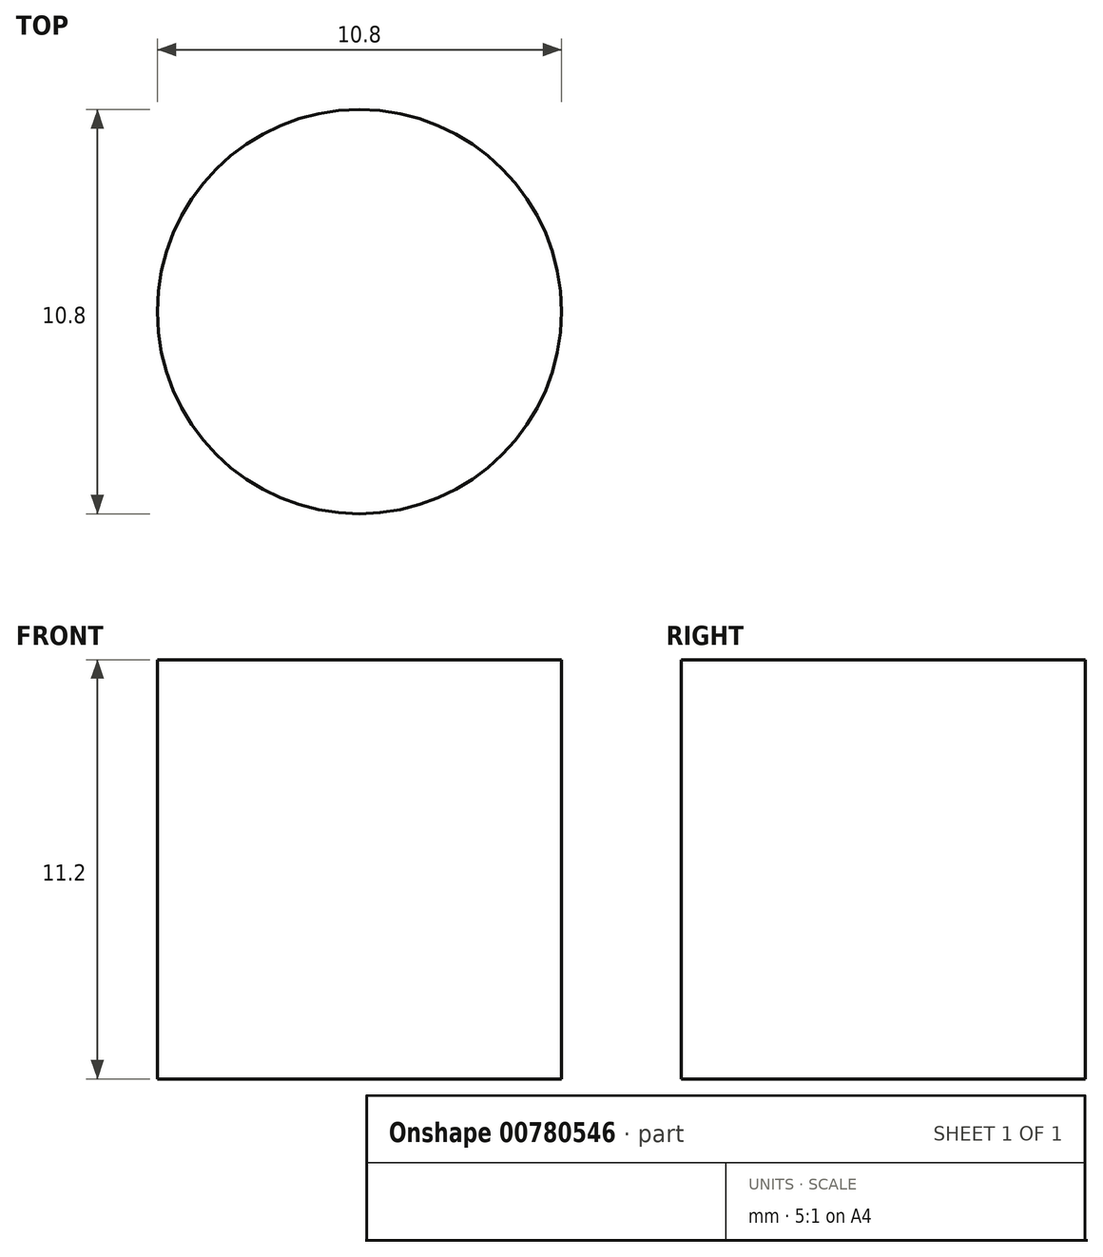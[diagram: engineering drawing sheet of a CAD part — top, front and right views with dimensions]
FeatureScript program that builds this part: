
annotation { "Feature Type Name" : "Feature", "Feature Type Description" : "" }
export const myFeature = defineFeature(function(context is Context, id is Id, definition is map)
    precondition{}
    {
        {
            var Q0;
            Q0=qCreatedBy(makeId("Top.planeOp"),FACE);
            var sketch = newSketch(context, id + "F0", { "sketchPlane" : qUnion([Q0])});
            skCircle(sketch, "E0", {"center": v(0, 0) * mm, "radius": 5.4 * mm});
            skSolve(sketch);
        }
        {
            var Q0;
            Q0=qSketchRegion(id+"F0",true);
            extrude(context, id + "F1", {"entities" : qUnion([Q0]), "depth" : 11.2 * mm, "offsetDistance" : 25 * mm});
        }
    });
